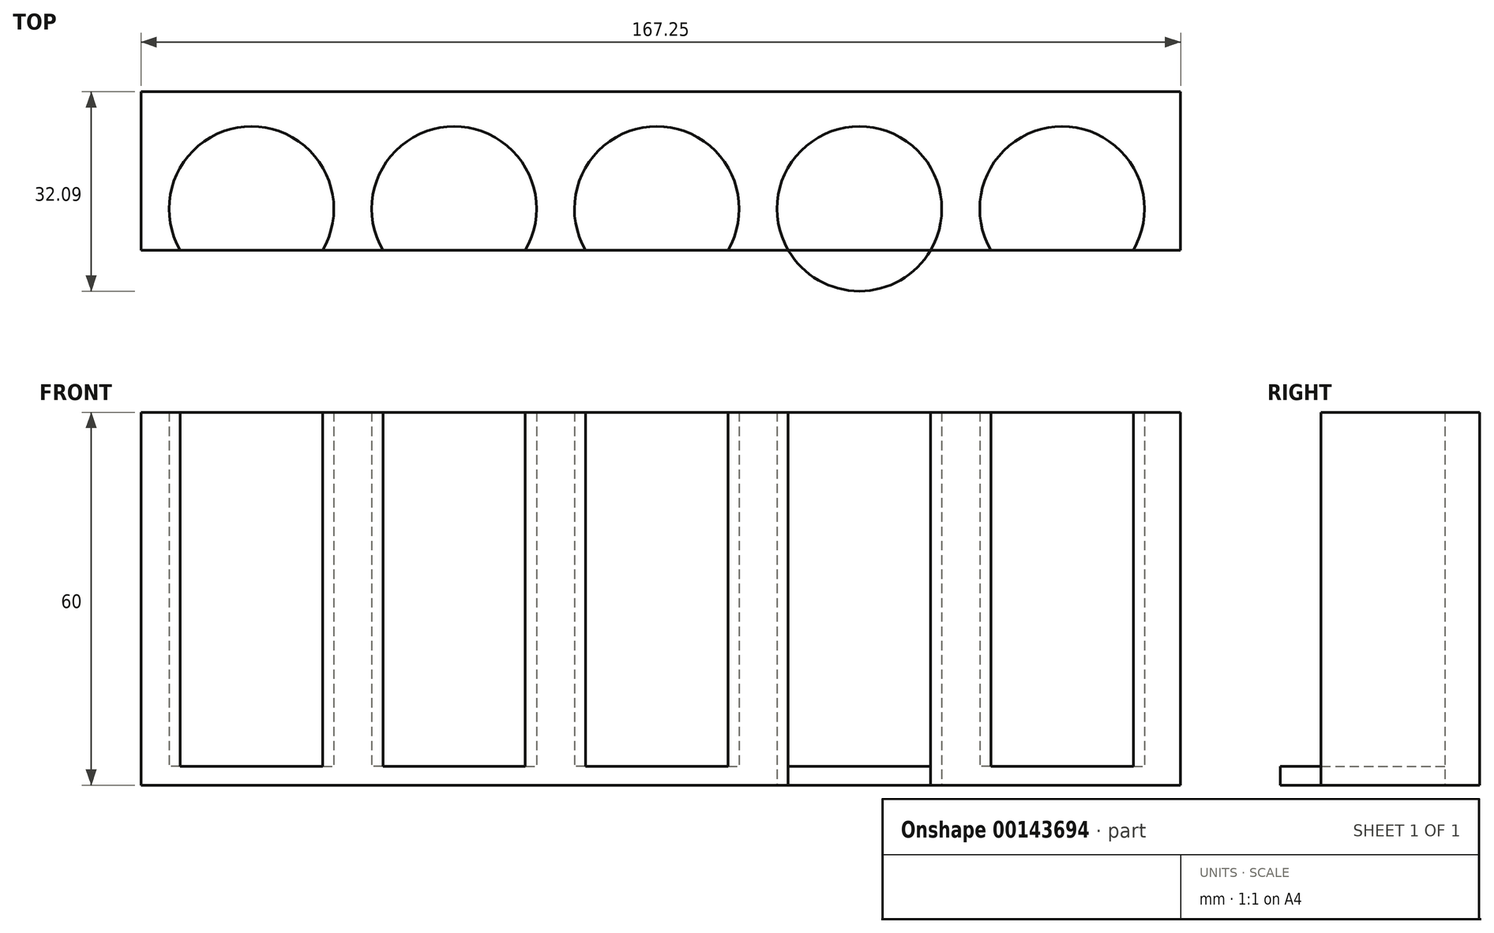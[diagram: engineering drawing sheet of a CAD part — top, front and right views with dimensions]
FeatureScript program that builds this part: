
annotation { "Feature Type Name" : "Feature", "Feature Type Description" : "" }
export const myFeature = defineFeature(function(context is Context, id is Id, definition is map)
    precondition{}
    {
        {
            var Q0;
            Q0=qCreatedBy(makeId("Top.planeOp"),FACE);
            var sketch = newSketch(context, id + "F0", { "sketchPlane" : qUnion([Q0])});
            skCircle(sketch, "E0", {"center": v(0, 6.65) * mm, "radius": 13.25 * mm});
            skCircle(sketch, "E1.1.0.0", {"center": v(32.6, 6.65) * mm, "radius": 13.25 * mm});
            skCircle(sketch, "E1.2.0.0", {"center": v(65.2, 6.65) * mm, "radius": 13.25 * mm});
            skCircle(sketch, "E1.3.0.0", {"center": v(97.8, 6.65) * mm, "radius": 13.25 * mm});
            skLineSegment(sketch, "E1.direction1", {"start": v(0, 6.65) * mm, "end": v(32.6, 6.65) * mm, "construction": true});
            skCircle(sketch, "E2.0.4.0", {"center": v(130.4, 6.65) * mm, "radius": 13.25 * mm});
            skLineSegment(sketch, "E3.bottom", {"start": v(-17.78, 0) * mm, "end": v(149.47, 0) * mm});
            skLineSegment(sketch, "E3.top", {"start": v(-17.78, 25.5) * mm, "end": v(149.47, 25.5) * mm});
            skLineSegment(sketch, "E3.left", {"start": v(-17.78, 0) * mm, "end": v(-17.78, 25.5) * mm});
            skLineSegment(sketch, "E3.right", {"start": v(149.47, 0) * mm, "end": v(149.47, 25.5) * mm});
            skSolve(sketch);
        }
        {
            var Q0;
            Q0=makeQuery(id+"F0.imprint","IMPRINT",FACE,{"disambiguationData":[TD([[makeQuery(id+"F0.imprint","IMPRINT",EDGE,{"derivedFrom":sQuery(id+"F0.wireOp",EDGE,"E3.top")}),-1.0]])]});
            var Q1;
            {var subQ0=sQuery(id+"F0.wireOp",EDGE,"E3.bottom");var subQ1=sQuery(id+"F0.wireOp",EDGE,"E0");var subQ2=makeQuery(id+"F0.imprint","INTERSECT",VERTEX,{"disambiguationData":[OD(0.0)],"derivedFrom":[subQ1,subQ0]});Q1=makeQuery(id+"F0.imprint","IMPRINT",FACE,{"disambiguationData":[TD([[makeQuery(id+"F0.imprint","IMPRINT",EDGE,{"disambiguationData":[TD([[subQ2,1.0]])],"derivedFrom":subQ1}),1.0]])]});}
            var Q2;
            {var subQ0=sQuery(id+"F0.wireOp",EDGE,"E3.bottom");var subQ1=sQuery(id+"F0.wireOp",EDGE,"E1.1.0.0");var subQ2=makeQuery(id+"F0.imprint","INTERSECT",VERTEX,{"disambiguationData":[OD(0.0)],"derivedFrom":[subQ1,subQ0]});Q2=makeQuery(id+"F0.imprint","IMPRINT",FACE,{"disambiguationData":[TD([[makeQuery(id+"F0.imprint","IMPRINT",EDGE,{"disambiguationData":[TD([[subQ2,1.0]])],"derivedFrom":subQ1}),1.0]])]});}
            var Q3;
            {var subQ0=sQuery(id+"F0.wireOp",EDGE,"E3.bottom");var subQ1=sQuery(id+"F0.wireOp",EDGE,"E1.2.0.0");var subQ2=makeQuery(id+"F0.imprint","INTERSECT",VERTEX,{"disambiguationData":[OD(0.0)],"derivedFrom":[subQ1,subQ0]});Q3=makeQuery(id+"F0.imprint","IMPRINT",FACE,{"disambiguationData":[TD([[makeQuery(id+"F0.imprint","IMPRINT",EDGE,{"disambiguationData":[TD([[subQ2,1.0]])],"derivedFrom":subQ1}),1.0]])]});}
            var Q4;
            {var subQ0=sQuery(id+"F0.wireOp",EDGE,"E3.bottom");var subQ1=sQuery(id+"F0.wireOp",EDGE,"E2.0.4.0");var subQ2=makeQuery(id+"F0.imprint","INTERSECT",VERTEX,{"disambiguationData":[OD(0.0)],"derivedFrom":[subQ1,subQ0]});Q4=makeQuery(id+"F0.imprint","IMPRINT",FACE,{"disambiguationData":[TD([[makeQuery(id+"F0.imprint","IMPRINT",EDGE,{"disambiguationData":[TD([[subQ2,1.0]])],"derivedFrom":subQ1}),1.0]])]});}
            var Q5;
            {var subQ0=sQuery(id+"F0.wireOp",EDGE,"E3.bottom");var subQ1=sQuery(id+"F0.wireOp",EDGE,"E1.3.0.0");var subQ2=makeQuery(id+"F0.imprint","INTERSECT",VERTEX,{"disambiguationData":[OD(0.0)],"derivedFrom":[subQ1,subQ0]});Q5=makeQuery(id+"F0.imprint","IMPRINT",FACE,{"disambiguationData":[TD([[makeQuery(id+"F0.imprint","IMPRINT",EDGE,{"disambiguationData":[TD([[subQ2,1.0]])],"derivedFrom":subQ1}),1.0]])]});}
            extrude(context, id + "F1", {"entities" : qUnion([Q0, Q1, Q2, Q3, Q4, Q5]), "depth" : 3 * mm, "offsetDistance" : 25 * mm});
        }
        {
            var Q0;
            Q0=makeQuery(id+"F0.imprint","IMPRINT",FACE,{"disambiguationData":[TD([[makeQuery(id+"F0.imprint","IMPRINT",EDGE,{"derivedFrom":sQuery(id+"F0.wireOp",EDGE,"E3.top")}),-1.0]])]});
            extrude(context, id + "F2", {"entities" : qUnion([Q0]), "operationType" : NewBodyOperationType.ADD, "flatOperationType" : FlatOperationType.REMOVE, "depth" : 60 * mm, "offsetDistance" : 25 * mm, "domain" : OperationDomain.MODEL});
        }
    });
